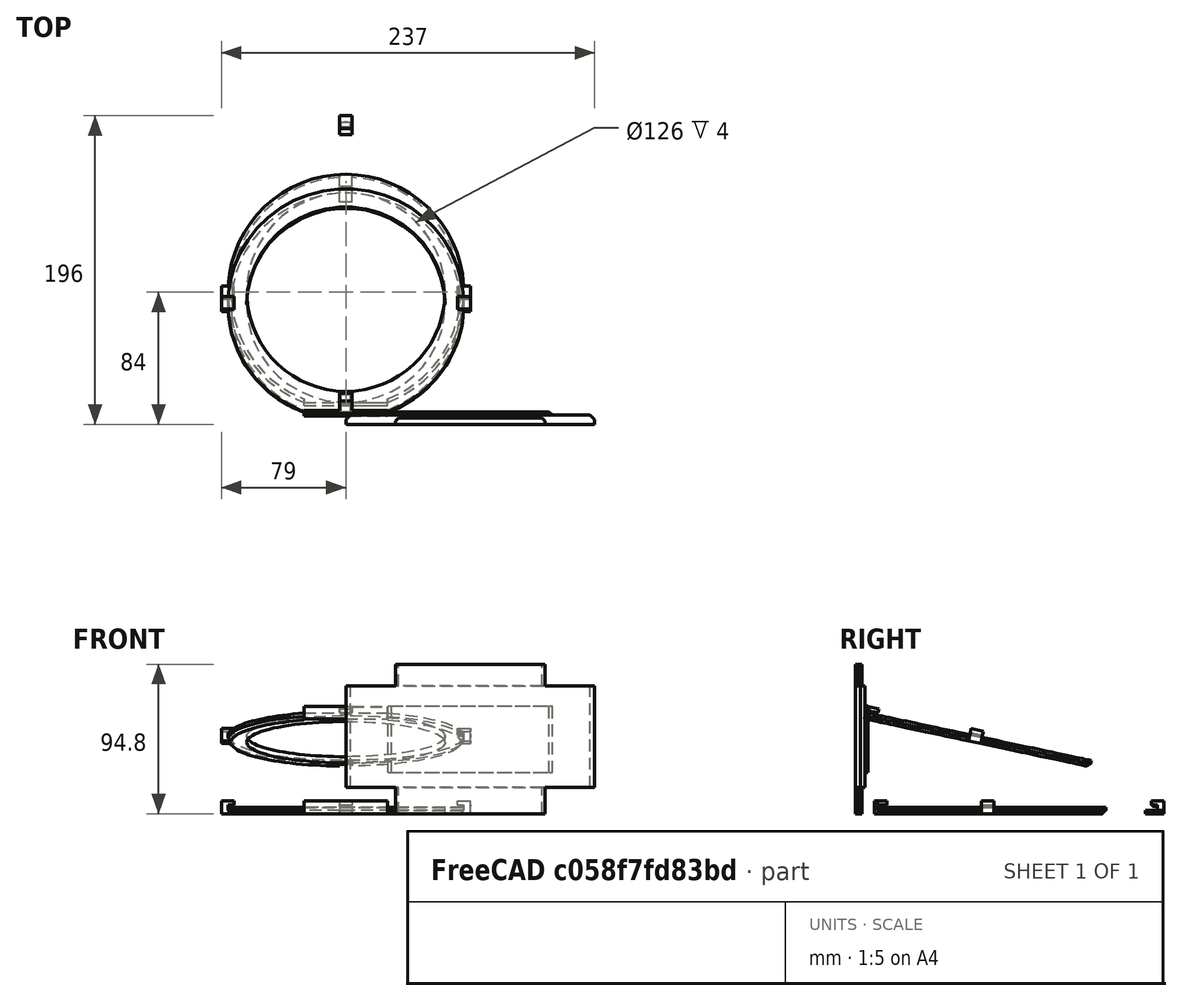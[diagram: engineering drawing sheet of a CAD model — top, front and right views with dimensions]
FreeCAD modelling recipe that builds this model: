
FCSTD DOCUMENT  (FreeCAD 0.19R0.19.2)
Label: waferHolder_012
License: All rights reserved
LicenseURL: http://en.wikipedia.org/wiki/All_rights_reserved
objects: Part::Box×31, Part::Chamfer×28, Part::Cut×10, Sketcher::SketchObject×7, Part::Extrusion×7, Part::MultiFuse×6
note: 89 computed .brp shape members not serialized (recipe doc carries the construction recipe); baked Part::Feature solids carry a one-line shape summary decoded from their .brp

FEATURE [Sketcher::SketchObject] Sketch
  FullyConstrained = true
  sketch-geometry (3):
    g0: Circle CenterX=-3.1415e-12 CenterY=5.6243e-12 CenterZ=0 NormalX=0 NormalY=0 NormalZ=1 AngleXU=0 Radius=63
    g1: ArcOfCircle CenterX=-3.1415e-12 CenterY=5.6243e-12 CenterZ=0 NormalX=0 NormalY=0 NormalZ=1 AngleXU=0 Radius=74.8482 StartAngle=5.07429 EndAngle=10.6337
    g2: LineSegment StartX=-26.5 StartY=-70.0001 StartZ=0 EndX=26.5 EndY=-70.0001 EndZ=0
  constraints (6):
    c: Block(g0)
    c: Coincident(g1,g0)
    c: Block(g1)
    c: Coincident(g2,g1)
    c: Coincident(g2,g1)
    c: Horizontal(g2)
FEATURE [Part::Box] Box  label="holderBitLeft"
  AttacherType = Attacher::AttachEngine3D
  Height = 4
  Length = 8
  Placement = pos=(-79,-4,0) rot=(0,0,1;0rad)
  Width = 8
FEATURE [Part::Box] Box001  label="bitHolderTopCutout"
  AttacherType = Attacher::AttachEngine3D
  Height = 4
  Length = 8
  Placement = pos=(-4,67,-2) rot=(0,0,1;0rad)
  Width = 12
FEATURE [Part::Extrusion] Extrude  label="mainHolderRing"
  Base = -> Sketch
  Dir = (0,0,1)
  DirMode = 2
  FaceMakerClass = Part::FaceMakerBullseye
  LengthFwd = 4
  LengthRev = 0
  Solid = true
  Symmetric = false
FEATURE [Part::Box] Box002  label="holderBitRight"
  AttacherType = Attacher::AttachEngine3D
  Height = 4
  Length = 8
  Placement = pos=(71,-4,0) rot=(0,0,1;0rad)
  Width = 8
FEATURE [Part::Box] Box003  label="bitHolderTop"
  AttacherType = Attacher::AttachEngine3D
  Height = 2
  Length = 8
  Placement = pos=(-4,100,0) rot=(0,0,1;0rad)
  Width = 12
FEATURE [Part::Chamfer] Chamfer
  Base = -> Extrude
  Edges = 1 edges r=2: [Edge3]
FEATURE [Part::Cut] Cut  label="mainHolderRing001"
  Base = -> Chamfer
  Tool = -> Box001
FEATURE [Part::Box] Box004  label="holderBitLeft001"
  AttacherType = Attacher::AttachEngine3D
  Height = 4
  Length = 6
  Placement = pos=(-79,-4,0) rot=(0,0,1;0rad)
  Width = 8
FEATURE [Part::Box] Box005  label="holderBitright002"
  AttacherType = Attacher::AttachEngine3D
  Height = 4
  Length = 6
  Placement = pos=(73,-4,0) rot=(0,0,1;0rad)
  Width = 8
FEATURE [Part::MultiFuse] Fusion  label="holders"
  Shapes = -> [Box004,Box005]
FEATURE [Sketcher::SketchObject] Sketch001
  FullyConstrained = true
  sketch-geometry (3):
    g0: Circle CenterX=-3.1415e-12 CenterY=5.6243e-12 CenterZ=0 NormalX=0 NormalY=0 NormalZ=1 AngleXU=0 Radius=63
    g1: ArcOfCircle CenterX=-3.1415e-12 CenterY=5.6243e-12 CenterZ=0 NormalX=0 NormalY=0 NormalZ=1 AngleXU=0 Radius=74.8482 StartAngle=5.07429 EndAngle=10.6337
    g2: LineSegment StartX=-26.5 StartY=-70.0001 StartZ=0 EndX=26.5 EndY=-70.0001 EndZ=0
  constraints (6):
    c: Block(g0)
    c: Coincident(g1,g0)
    c: Block(g1)
    c: Coincident(g2,g1)
    c: Coincident(g2,g1)
    c: Horizontal(g2)
FEATURE [Part::Extrusion] Extrude001  label="mainHolderRing002"
  Base = -> Sketch001
  Dir = (0,0,1)
  DirMode = 2
  FaceMakerClass = Part::FaceMakerBullseye
  LengthFwd = 4
  LengthRev = 0
  Solid = true
  Symmetric = false
FEATURE [Part::Cut] Cut001  label="leftAndRightHolderBits"
  Base = -> Fusion
  Placement = pos=(0,0,4) rot=(0,0,1;0rad)
  Tool = -> Extrude001
FEATURE [Part::Box] Box006  label="holderBitLeft002"
  AttacherType = Attacher::AttachEngine3D
  Height = 3.4
  Length = 8
  Placement = pos=(-79,-4,4.6) rot=(0,0,1;0rad)
  Width = 8
FEATURE [Part::Box] Box007  label="holderBitRight002"
  AttacherType = Attacher::AttachEngine3D
  Height = 3.4
  Length = 8
  Placement = pos=(71,-4,4.6) rot=(0,0,1;0rad)
  Width = 8
FEATURE [Part::Box] Box008  label="holderBitLeft003"
  AttacherType = Attacher::AttachEngine3D
  Height = 2
  Length = 8
  Placement = pos=(-4,71,2) rot=(0,0,1;0rad)
  Width = 8
FEATURE [Part::Box] Box009  label="bitHolderTopCutout001"
  AttacherType = Attacher::AttachEngine3D
  Height = 4
  Length = 8
  Placement = pos=(-4,67,-2) rot=(0,0,1;0rad)
  Width = 12
FEATURE [Sketcher::SketchObject] Sketch002
  FullyConstrained = true
  sketch-geometry (3):
    g0: Circle CenterX=-3.1415e-12 CenterY=5.6243e-12 CenterZ=0 NormalX=0 NormalY=0 NormalZ=1 AngleXU=0 Radius=63
    g1: ArcOfCircle CenterX=-3.1415e-12 CenterY=5.6243e-12 CenterZ=0 NormalX=0 NormalY=0 NormalZ=1 AngleXU=0 Radius=74.8482 StartAngle=5.07429 EndAngle=10.6337
    g2: LineSegment StartX=-26.5 StartY=-70.0001 StartZ=0 EndX=26.5 EndY=-70.0001 EndZ=0
  constraints (6):
    c: Block(g0)
    c: Coincident(g1,g0)
    c: Block(g1)
    c: Coincident(g2,g1)
    c: Coincident(g2,g1)
    c: Horizontal(g2)
FEATURE [Part::Extrusion] Extrude002  label="mainHolderRing003"
  Base = -> Sketch002
  Dir = (0,0,1)
  DirMode = 2
  FaceMakerClass = Part::FaceMakerBullseye
  LengthFwd = 4
  LengthRev = 0
  Solid = true
  Symmetric = false
FEATURE [Part::Chamfer] Chamfer001
  Base = -> Extrude002
  Edges = 1 edges r=2: [Edge3]
FEATURE [Part::Cut] Cut002  label="mainHolderRing004"
  Base = -> Chamfer001
  Tool = -> Box009
FEATURE [Part::Cut] Cut003  label="bitHolderTop001"
  Base = -> Box008
  Tool = -> Cut002
FEATURE [Part::Box] Box010  label="holderBitLeft004"
  AttacherType = Attacher::AttachEngine3D
  Height = 2
  Length = 8
  Placement = pos=(-4,71,2) rot=(0,0,1;0rad)
  Width = 8
FEATURE [Part::Box] Box011  label="bitHolderTopCutout002"
  AttacherType = Attacher::AttachEngine3D
  Height = 4
  Length = 8
  Placement = pos=(-4,67,-2) rot=(0,0,1;0rad)
  Width = 12
FEATURE [Sketcher::SketchObject] Sketch003
  FullyConstrained = true
  sketch-geometry (3):
    g0: Circle CenterX=-3.1415e-12 CenterY=5.6243e-12 CenterZ=0 NormalX=0 NormalY=0 NormalZ=1 AngleXU=0 Radius=63
    g1: ArcOfCircle CenterX=-3.1415e-12 CenterY=5.6243e-12 CenterZ=0 NormalX=0 NormalY=0 NormalZ=1 AngleXU=0 Radius=74.8482 StartAngle=5.07429 EndAngle=10.6337
    g2: LineSegment StartX=-26.5 StartY=-70.0001 StartZ=0 EndX=26.5 EndY=-70.0001 EndZ=0
  constraints (6):
    c: Block(g0)
    c: Coincident(g1,g0)
    c: Block(g1)
    c: Coincident(g2,g1)
    c: Coincident(g2,g1)
    c: Horizontal(g2)
FEATURE [Part::Extrusion] Extrude003  label="mainHolderRing006"
  Base = -> Sketch003
  Dir = (0,0,1)
  DirMode = 2
  FaceMakerClass = Part::FaceMakerBullseye
  LengthFwd = 4
  LengthRev = 0
  Solid = true
  Symmetric = false
FEATURE [Part::Chamfer] Chamfer002
  Base = -> Extrude003
  Edges = 1 edges r=2: [Edge3]
FEATURE [Part::Cut] Cut005  label="mainHolderRing005"
  Base = -> Chamfer002
  Tool = -> Box011
FEATURE [Part::Cut] Cut004  label="bitHolderTop002"
  Base = -> Box010
  Placement = pos=(0,0,2) rot=(0,0,1;0rad)
  Tool = -> Cut005
FEATURE [Part::Box] Box012  label="holderBitLeft005"
  AttacherType = Attacher::AttachEngine3D
  Height = 2
  Length = 8
  Placement = pos=(-4,71,2) rot=(0,0,1;0rad)
  Width = 8
FEATURE [Part::Box] Box013  label="bitHolderTopCutout003"
  AttacherType = Attacher::AttachEngine3D
  Height = 4
  Length = 8
  Placement = pos=(-4,67,-2) rot=(0,0,1;0rad)
  Width = 12
FEATURE [Sketcher::SketchObject] Sketch004
  FullyConstrained = true
  sketch-geometry (3):
    g0: Circle CenterX=-3.1415e-12 CenterY=5.6243e-12 CenterZ=0 NormalX=0 NormalY=0 NormalZ=1 AngleXU=0 Radius=63
    g1: ArcOfCircle CenterX=-3.1415e-12 CenterY=5.6243e-12 CenterZ=0 NormalX=0 NormalY=0 NormalZ=1 AngleXU=0 Radius=74.8482 StartAngle=5.07429 EndAngle=10.6337
    g2: LineSegment StartX=-26.5 StartY=-70.0001 StartZ=0 EndX=26.5 EndY=-70.0001 EndZ=0
  constraints (6):
    c: Block(g0)
    c: Coincident(g1,g0)
    c: Block(g1)
    c: Coincident(g2,g1)
    c: Coincident(g2,g1)
    c: Horizontal(g2)
FEATURE [Part::Extrusion] Extrude004  label="mainHolderRing008"
  Base = -> Sketch004
  Dir = (0,0,1)
  DirMode = 2
  FaceMakerClass = Part::FaceMakerBullseye
  LengthFwd = 4
  LengthRev = 0
  Solid = true
  Symmetric = false
FEATURE [Part::Chamfer] Chamfer003
  Base = -> Extrude004
  Edges = 1 edges r=2: [Edge3]
FEATURE [Part::Cut] Cut007  label="mainHolderRing007"
  Base = -> Chamfer003
  Tool = -> Box013
FEATURE [Part::Cut] Cut006  label="bitHolderTop003"
  Base = -> Box012
  Placement = pos=(0,0,4) rot=(0,0,1;0rad)
  Tool = -> Cut007
FEATURE [Part::Box] Box014  label="bitHoldertop006"
  AttacherType = Attacher::AttachEngine3D
  Height = 3.4
  Length = 8
  Placement = pos=(-4,71,4.6) rot=(0,0,1;0rad)
  Width = 8
FEATURE [Part::MultiFuse] Fusion001  label="holderTop"
  Placement = pos=(0,33,0) rot=(0,0,1;0rad)
  Shapes = -> [Cut003,Cut004,Cut006,Box014]
FEATURE [Part::Chamfer] Chamfer004
  Base = -> Fusion001
  Edges = 1 edges r=1: [Edge16]
FEATURE [Part::Chamfer] Chamfer005
  Base = -> Box006
  Edges = 1 edges r=1: [Edge8]
FEATURE [Part::Chamfer] Chamfer006
  Base = -> Box007
  Edges = 1 edges r=1: [Edge4]
FEATURE [Part::Chamfer] Chamfer007
  Base = -> Chamfer006
  Edges = 1 edges r=1: [Edge13]
FEATURE [Part::Chamfer] Chamfer008
  Base = -> Chamfer007
  Edges = 1 edges r=1: [Edge5]
FEATURE [Part::Chamfer] Chamfer009
  Base = -> Chamfer004
  Edges = 1 edges r=1: [Edge1]
FEATURE [Part::Chamfer] Chamfer010
  Base = -> Chamfer009
  Edges = 1 edges r=1: [Edge32]
FEATURE [Part::Chamfer] Chamfer011
  Base = -> Chamfer005
  Edges = 1 edges r=1: [Edge5]
FEATURE [Part::Chamfer] Chamfer012
  Base = -> Chamfer011
  Edges = 1 edges r=1: [Edge16]
FEATURE [Part::Box] Box015  label="holderBottom"
  AttacherType = Attacher::AttachEngine3D
  Height = 4
  Length = 53
  Placement = pos=(-26.5,-72,0) rot=(0,0,1;0rad)
  Width = 4.5
FEATURE [Part::Box] Box016  label="holderBottom001"
  AttacherType = Attacher::AttachEngine3D
  Height = 4
  Length = 53
  Placement = pos=(-26.5,-72,4) rot=(0,0,1;0rad)
  Width = 2
FEATURE [Part::Box] Box017  label="holderBottom002"
  AttacherType = Attacher::AttachEngine3D
  Height = 3.4
  Length = 8
  Placement = pos=(-4,-72,4.6) rot=(0,0,1;0rad)
  Width = 8
FEATURE [Part::Chamfer] Chamfer013  label="holderBottom003"
  Base = -> Box017
  Edges = 3 edges r=1: [Edge4,Edge8,Edge11]
FEATURE [Part::Box] Box018  label="base001"
  AttacherType = Attacher::AttachEngine3D
  Height = 64.44
  Length = 158
  Placement = pos=(0,-84,16.6) rot=(0,0,1;0rad)
  Width = 6
FEATURE [Part::Box] Box019  label="base002"
  AttacherType = Attacher::AttachEngine3D
  Height = 94.8
  Length = 94.8
  Placement = pos=(31.6,-84,0) rot=(0,0,1;0rad)
  Width = 4
FEATURE [Part::Box] Box020  label="base003"
  AttacherType = Attacher::AttachEngine3D
  Height = 42.44
  Length = 104.28
  Placement = pos=(26.86,-84,26.18) rot=(0,0,1;0rad)
  Width = 8
FEATURE [Part::Chamfer] Chamfer014
  Base = -> Box018
  Edges = 1 edges r=3: [Edge3]
FEATURE [Part::Chamfer] Chamfer015
  Base = -> Chamfer014
  Edges = 1 edges r=3: [Edge15]
FEATURE [Part::Chamfer] Chamfer016
  Base = -> Box019
  Edges = 1 edges r=2: [Edge3]
FEATURE [Part::Chamfer] Chamfer017
  Base = -> Box020
  Edges = 1 edges r=2: [Edge3]
FEATURE [Part::Chamfer] Chamfer018
  Base = -> Chamfer016
  Edges = 1 edges r=2: [Edge15]
FEATURE [Part::Chamfer] Chamfer019
  Base = -> Chamfer017
  Edges = 1 edges r=2: [Edge15]
FEATURE [Part::MultiFuse] Fusion002  label="base004"
  Shapes = -> [Chamfer015,Chamfer018,Chamfer019]
FEATURE [Part::MultiFuse] Fusion003  label="ringHolder"
  Shapes = -> [Box,Box002,Cut,Cut001,Chamfer008,Chamfer012,Box015,Box016,Chamfer013]
FEATURE [Part::Box] Box021  label="holderBitLeft006"
  AttacherType = Attacher::AttachEngine3D
  Height = 4
  Length = 6
  Placement = pos=(-79,-4,0) rot=(0,0,1;0rad)
  Width = 8
FEATURE [Part::Box] Box022  label="holderBitright003"
  AttacherType = Attacher::AttachEngine3D
  Height = 4
  Length = 6
  Placement = pos=(73,-4,0) rot=(0,0,1;0rad)
  Width = 8
FEATURE [Part::Box] Box023  label="holderBitLeft007"
  AttacherType = Attacher::AttachEngine3D
  Height = 3.4
  Length = 8
  Placement = pos=(-79,-4,4.6) rot=(0,0,1;0rad)
  Width = 8
FEATURE [Part::Box] Box024  label="holderBitRight003"
  AttacherType = Attacher::AttachEngine3D
  Height = 3.4
  Length = 8
  Placement = pos=(71,-4,4.6) rot=(0,0,1;0rad)
  Width = 8
FEATURE [Sketcher::SketchObject] Sketch005
  FullyConstrained = true
  sketch-geometry (3):
    g0: Circle CenterX=-3.1415e-12 CenterY=5.6243e-12 CenterZ=0 NormalX=0 NormalY=0 NormalZ=1 AngleXU=0 Radius=63
    g1: ArcOfCircle CenterX=-3.1415e-12 CenterY=5.6243e-12 CenterZ=0 NormalX=0 NormalY=0 NormalZ=1 AngleXU=0 Radius=74.8482 StartAngle=5.07429 EndAngle=10.6337
    g2: LineSegment StartX=-26.5 StartY=-70.0001 StartZ=0 EndX=26.5 EndY=-70.0001 EndZ=0
  constraints (6):
    c: Block(g0)
    c: Coincident(g1,g0)
    c: Block(g1)
    c: Coincident(g2,g1)
    c: Coincident(g2,g1)
    c: Horizontal(g2)
FEATURE [Part::Box] Box025  label="holderBitLeft008"
  AttacherType = Attacher::AttachEngine3D
  Height = 4
  Length = 8
  Placement = pos=(-79,-4,0) rot=(0,0,1;0rad)
  Width = 8
FEATURE [Part::Box] Box026  label="bitHolderTopCutout004"
  AttacherType = Attacher::AttachEngine3D
  Height = 4
  Length = 8
  Placement = pos=(-4,67,-2) rot=(0,0,1;0rad)
  Width = 12
FEATURE [Part::Extrusion] Extrude006  label="mainHolderRing010"
  Base = -> Sketch005
  Dir = (0,0,1)
  DirMode = 2
  FaceMakerClass = Part::FaceMakerBullseye
  LengthFwd = 4
  LengthRev = 0
  Solid = true
  Symmetric = false
FEATURE [Part::Box] Box027  label="holderBitRight004"
  AttacherType = Attacher::AttachEngine3D
  Height = 4
  Length = 8
  Placement = pos=(71,-4,0) rot=(0,0,1;0rad)
  Width = 8
FEATURE [Part::Chamfer] Chamfer020
  Base = -> Extrude006
  Edges = 1 edges r=2: [Edge3]
FEATURE [Part::Cut] Cut008  label="mainHolderRing011"
  Base = -> Chamfer020
  Tool = -> Box026
FEATURE [Part::MultiFuse] Fusion004  label="holders001"
  Shapes = -> [Box021,Box022]
FEATURE [Sketcher::SketchObject] Sketch006
  FullyConstrained = true
  sketch-geometry (3):
    g0: Circle CenterX=-3.1415e-12 CenterY=5.6243e-12 CenterZ=0 NormalX=0 NormalY=0 NormalZ=1 AngleXU=0 Radius=63
    g1: ArcOfCircle CenterX=-3.1415e-12 CenterY=5.6243e-12 CenterZ=0 NormalX=0 NormalY=0 NormalZ=1 AngleXU=0 Radius=74.8482 StartAngle=5.07429 EndAngle=10.6337
    g2: LineSegment StartX=-26.5 StartY=-70.0001 StartZ=0 EndX=26.5 EndY=-70.0001 EndZ=0
  constraints (6):
    c: Block(g0)
    c: Coincident(g1,g0)
    c: Block(g1)
    c: Coincident(g2,g1)
    c: Coincident(g2,g1)
    c: Horizontal(g2)
FEATURE [Part::Extrusion] Extrude005  label="mainHolderRing009"
  Base = -> Sketch006
  Dir = (0,0,1)
  DirMode = 2
  FaceMakerClass = Part::FaceMakerBullseye
  LengthFwd = 4
  LengthRev = 0
  Solid = true
  Symmetric = false
FEATURE [Part::Cut] Cut009  label="leftAndRightHolderBits001"
  Base = -> Fusion004
  Placement = pos=(0,0,4) rot=(0,0,1;0rad)
  Tool = -> Extrude005
FEATURE [Part::Chamfer] Chamfer021
  Base = -> Box023
  Edges = 1 edges r=1: [Edge8]
FEATURE [Part::Chamfer] Chamfer022
  Base = -> Box024
  Edges = 1 edges r=1: [Edge4]
FEATURE [Part::Chamfer] Chamfer023
  Base = -> Chamfer022
  Edges = 1 edges r=1: [Edge13]
FEATURE [Part::Chamfer] Chamfer024
  Base = -> Chamfer023
  Edges = 1 edges r=1: [Edge5]
FEATURE [Part::Box] Box028  label="holderBottom004"
  AttacherType = Attacher::AttachEngine3D
  Height = 4
  Length = 53
  Placement = pos=(-26.5,-72,0) rot=(0,0,1;0rad)
  Width = 4.5
FEATURE [Part::Chamfer] Chamfer025
  Base = -> Chamfer021
  Edges = 1 edges r=1: [Edge5]
FEATURE [Part::Chamfer] Chamfer026
  Base = -> Chamfer025
  Edges = 1 edges r=1: [Edge16]
FEATURE [Part::Box] Box029  label="holderBottom006"
  AttacherType = Attacher::AttachEngine3D
  Height = 4
  Length = 53
  Placement = pos=(-26.5,-72,4) rot=(0,0,1;0rad)
  Width = 2
FEATURE [Part::Box] Box030  label="holderBottom007"
  AttacherType = Attacher::AttachEngine3D
  Height = 3.4
  Length = 8
  Placement = pos=(-4,-72,4.6) rot=(0,0,1;0rad)
  Width = 8
FEATURE [Part::Chamfer] Chamfer027  label="holderBottom005"
  Base = -> Box030
  Edges = 3 edges r=1: [Edge4,Edge8,Edge11]
FEATURE [Part::MultiFuse] Fusion005  label="ringHolder001"
  Placement = pos=(0,-8.35,45.4) rot=(1,0,0;6.07375rad)
  Shapes = -> [Box025,Box027,Cut008,Cut009,Chamfer024,Chamfer026,Box028,Box029,Chamfer027]
